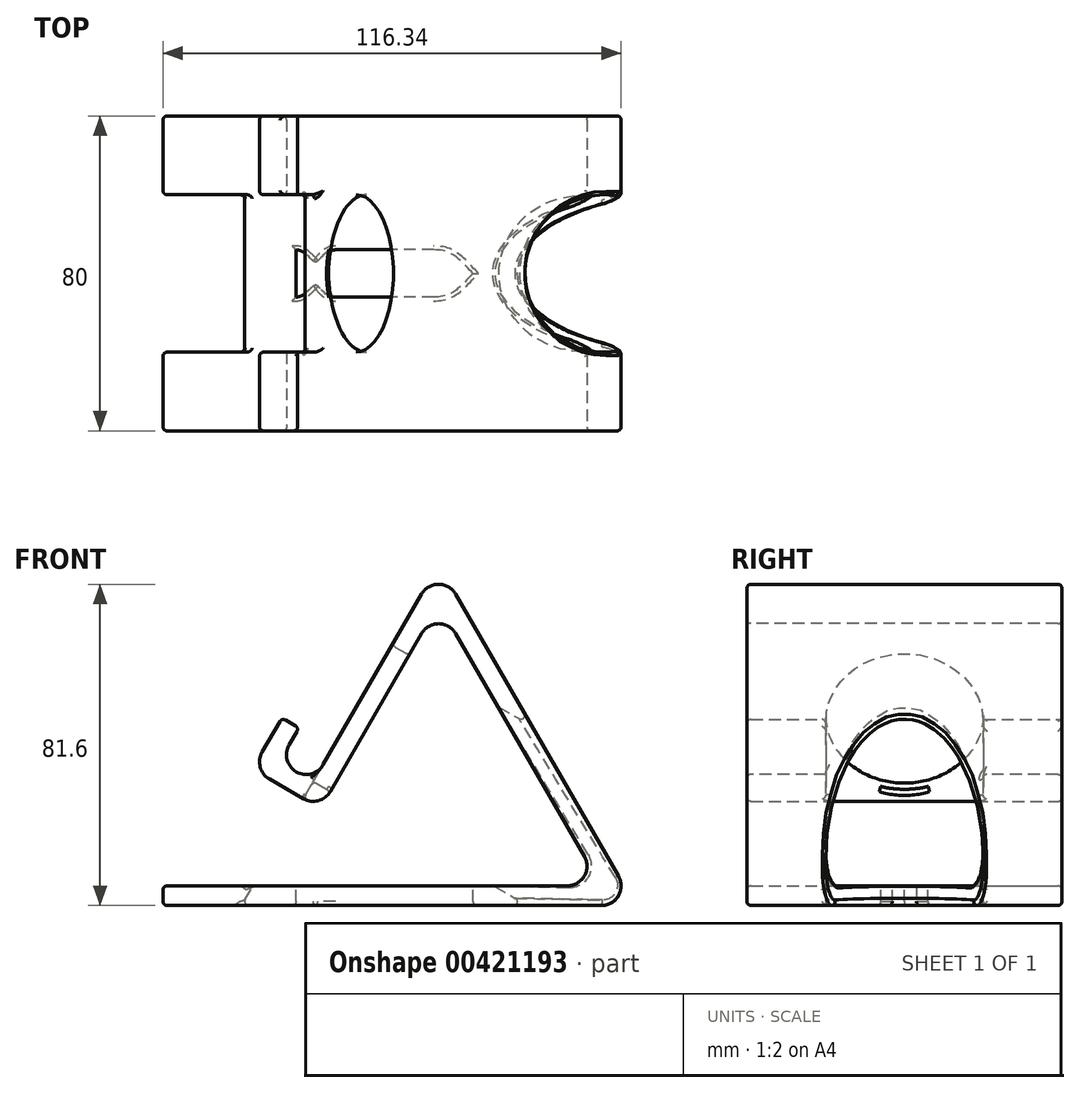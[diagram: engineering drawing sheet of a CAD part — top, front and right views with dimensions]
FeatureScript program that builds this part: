
annotation { "Feature Type Name" : "Feature", "Feature Type Description" : "" }
export const myFeature = defineFeature(function(context is Context, id is Id, definition is map)
    precondition{}
    {
        {
            var Q0;
            Q0=qCreatedBy(makeId("Front.planeOp"),FACE);
            var sketch = newSketch(context, id + "F0", { "sketchPlane" : qUnion([Q0])});
            skLineSegment(sketch, "E0", {"start": v(-70, -45.78) * mm, "end": v(50, -45.78) * mm});
            skLineSegment(sketch, "E1", {"start": v(50, -45.78) * mm, "end": v(0, 40.82) * mm});
            skLineSegment(sketch, "E2", {"start": v(0, 40.82) * mm, "end": v(-31.83, -14.3) * mm});
            skLineSegment(sketch, "E3", {"start": v(-31.83, -14.3) * mm, "end": v(-40.5, -9.3) * mm});
            skLineSegment(sketch, "E4", {"start": v(-40.5, -9.3) * mm, "end": v(-35.5, -0.65) * mm});
            skLineSegment(sketch, "E5", {"start": v(-35.5, -0.65) * mm, "end": v(-39.82, 1.85) * mm});
            skLineSegment(sketch, "E6", {"start": v(-39.82, 1.85) * mm, "end": v(-47.32, -11.14) * mm});
            skLineSegment(sketch, "E7", {"start": v(-47.32, -11.14) * mm, "end": v(-30, -21.14) * mm});
            skLineSegment(sketch, "E8", {"start": v(-30, -21.14) * mm, "end": v(0, 30.82) * mm});
            skLineSegment(sketch, "E9", {"start": v(0, 30.82) * mm, "end": v(41.34, -40.78) * mm});
            skLineSegment(sketch, "E10", {"start": v(41.34, -40.78) * mm, "end": v(-70, -40.78) * mm});
            skLineSegment(sketch, "E11", {"start": v(-70, -40.78) * mm, "end": v(-70, -45.78) * mm});
            skSolve(sketch);
        }
        {
            var Q0;
            Q0=makeQuery(id+"F0.imprint","IMPRINT",FACE,{"disambiguationData":[TD([[makeQuery(id+"F0.imprint","IMPRINT",EDGE,{"derivedFrom":sQuery(id+"F0.wireOp",EDGE,"E0")}),1.0]])]});
            extrude(context, id + "F1", {"entities" : qUnion([Q0]), "depth" : 80 * mm, "offsetDistance" : 25 * mm});
        }
        {
            var Q0;
            Q0=makeQuery(id+"F1.opExtrude","SWEPT_FACE",FACE,{"disambiguationData":[OSD([sQuery(id+"F0.wireOp",EDGE,"E3")])]});
            var sketch = newSketch(context, id + "F2", { "sketchPlane" : qUnion([Q0])});
            skLineSegment(sketch, "E12", {"start": v(-30.41, -40) * mm, "end": v(-20.41, -40) * mm});
            skLineSegment(sketch, "E13", {"start": v(-30.41, -40) * mm, "end": v(-30.41, -20) * mm});
            skLineSegment(sketch, "E14", {"start": v(-30.41, -20) * mm, "end": v(-20.41, -20) * mm});
            skLineSegment(sketch, "E15", {"start": v(-20.41, -20) * mm, "end": v(-20.41, -40) * mm});
            skLineSegment(sketch, "E16.MirrorCS", {"start": v(-20.41, -60) * mm, "end": v(-20.41, -40) * mm});
            skLineSegment(sketch, "E17.MirrorCS", {"start": v(-30.41, -40) * mm, "end": v(-30.41, -60) * mm});
            skLineSegment(sketch, "E18.MirrorCS", {"start": v(-30.41, -60) * mm, "end": v(-20.41, -60) * mm});
            skLineSegment(sketch, "E19", {"start": v(-30.41, -60) * mm, "end": v(-57.62, -60) * mm});
            skLineSegment(sketch, "E20", {"start": v(-57.62, -60) * mm, "end": v(-57.62, -20) * mm});
            skLineSegment(sketch, "E21", {"start": v(-57.62, -20) * mm, "end": v(-30.41, -20) * mm});
            skSolve(sketch);
        }
        {
            var Q0;
            Q0=makeQuery(id+"F2.imprint","IMPRINT",FACE,{"disambiguationData":[TD([[makeQuery(id+"F2.imprint","IMPRINT",EDGE,{"derivedFrom":sQuery(id+"F2.wireOp",EDGE,"E12")}),1.0]])]});
            var Q1;
            Q1=makeQuery(id+"F2.imprint","IMPRINT",FACE,{"disambiguationData":[TD([[makeQuery(id+"F2.imprint","IMPRINT",EDGE,{"derivedFrom":sQuery(id+"F2.wireOp",EDGE,"E12")}),-1.0]])]});
            var Q2;
            Q2=makeQuery(id+"F2.imprint","IMPRINT",FACE,{"disambiguationData":[TD([[makeQuery(id+"F2.imprint","IMPRINT",EDGE,{"derivedFrom":sQuery(id+"F2.wireOp",EDGE,"E13")}),1.0]])]});
            extrude(context, id + "F3", {"entities" : qUnion([Q0, Q1, Q2]), "operationType" : NewBodyOperationType.REMOVE, "oppositeDirection" : true, "depth" : 67.1 * mm, "offsetDistance" : 25 * mm, "hasSecondDirection" : true, "secondDirectionOppositeDirection" : false, "secondDirectionDepth" : 25 * mm});
        }
        {
            var Q0;
            Q0=makeQuery(id+"F1.opExtrude","SWEPT_FACE",FACE,{"disambiguationData":[OSD([sQuery(id+"F0.wireOp",EDGE,"E8")])]});
            var sketch = newSketch(context, id + "F4", { "sketchPlane" : qUnion([Q0])});
            skCircle(sketch, "E22", {"center": v(-40, -8.3) * mm, "radius": 20 * mm});
            skPoint(sketch, "E22.centerSnap0", {"position": v(-40, 26.7) * mm});
            skSolve(sketch);
        }
        {
            var Q0;
            Q0=makeQuery(id+"F4.imprint","IMPRINT",FACE,{"disambiguationData":[TD([[makeQuery(id+"F4.imprint","IMPRINT",EDGE,{"derivedFrom":sQuery(id+"F4.wireOp",EDGE,"E22")}),1.0]])]});
            extrude(context, id + "F5", {"entities" : qUnion([Q0]), "operationType" : NewBodyOperationType.REMOVE, "oppositeDirection" : true, "depth" : 25 * mm, "offsetDistance" : 25 * mm, "hasSecondDirection" : true, "secondDirectionOppositeDirection" : false, "secondDirectionDepth" : 129.4 * mm});
        }
        {
            var Q0;
            Q0=makeQuery(id+"F1.opExtrude","SWEPT_FACE",FACE,{"disambiguationData":[OSD([sQuery(id+"F0.wireOp",EDGE,"E10")])]});
            var sketch = newSketch(context, id + "F6", { "sketchPlane" : qUnion([Q0])});
            skPoint(sketch, "E23.0.internal.snap0", {"position": v(13.75, -40) * mm});
            skFitSpline(sketch, "E23", {"points": [v(8.75, -40) * mm, v(-1.25, -46) * mm], "startDerivative": vector(-10.6, -10.6) * mm, "endDerivative": vector(-15, 0) * mm});
            skLineSegment(sketch, "E24", {"start": v(8.75, -40) * mm, "end": v(-36.25, -40) * mm});
            skLineSegment(sketch, "E25", {"start": v(-1.25, -46) * mm, "end": v(-26.25, -46) * mm});
            skFitSpline(sketch, "E26", {"points": [v(-26.25, -46) * mm, v(-31.25, -43) * mm, v(-36.25, -46) * mm], "startDerivative": vector(-18, 0) * mm, "endDerivative": vector(-15, 0) * mm});
            skLineSegment(sketch, "E27", {"start": v(-36.25, -46) * mm, "end": v(-36.25, -40) * mm});
            skLineSegment(sketch, "E28", {"start": v(5.22, -43.54) * mm, "end": v(8.75, -40) * mm});
            skLineSegment(sketch, "E29.MirrorCS", {"start": v(5.22, -36.46) * mm, "end": v(8.75, -40) * mm});
            skFitSpline(sketch, "E30.MirrorCS", {"points": [v(-26.25, -34) * mm, v(-31.25, -37) * mm, v(-36.25, -34) * mm], "startDerivative": vector(-18, 0) * mm, "endDerivative": vector(-15, 0) * mm});
            skLineSegment(sketch, "E31.MirrorCS", {"start": v(-1.25, -34) * mm, "end": v(-26.25, -34) * mm});
            skLineSegment(sketch, "E32.MirrorCS", {"start": v(-36.25, -34) * mm, "end": v(-36.25, -40) * mm});
            skFitSpline(sketch, "E33.MirrorCS", {"points": [v(8.75, -40) * mm, v(-1.25, -34) * mm], "startDerivative": vector(-10.6, 10.6) * mm, "endDerivative": vector(-15, 0) * mm});
            skSolve(sketch);
        }
        {
            var Q0;
            Q0=makeQuery(id+"F6.imprint","IMPRINT",FACE,{"disambiguationData":[TD([[makeQuery(id+"F6.imprint","IMPRINT",EDGE,{"derivedFrom":sQuery(id+"F6.wireOp",EDGE,"E24")}),-1.0]])]});
            var Q1;
            Q1=makeQuery(id+"F6.imprint","IMPRINT",FACE,{"disambiguationData":[TD([[makeQuery(id+"F6.imprint","IMPRINT",EDGE,{"derivedFrom":sQuery(id+"F6.wireOp",EDGE,"E23")}),-1.0]])]});
            extrude(context, id + "F7", {"entities" : qUnion([Q0, Q1]), "operationType" : NewBodyOperationType.REMOVE, "oppositeDirection" : true, "depth" : 25 * mm, "offsetDistance" : 25 * mm});
        }
        {
            var Q0;
            Q0=makeQuery(id+"F1.opExtrude","SWEPT_EDGE",EDGE,{"disambiguationData":[OSD([sQuery(id+"F0.wireOp",EDGE,"E1"),sQuery(id+"F0.wireOp",EDGE,"E2")])]});
            var Q1;
            Q1=makeQuery(id+"F1.opExtrude","SWEPT_EDGE",EDGE,{"disambiguationData":[OSD([sQuery(id+"F0.wireOp",EDGE,"E8"),sQuery(id+"F0.wireOp",EDGE,"E9")])]});
            var Q2;
            {var subQ0=sQuery(id+"F0.wireOp",EDGE,"E0");var subQ1=sQuery(id+"F0.wireOp",EDGE,"E1");Q2=makeQuery(id+"F5.boolean.opBoolean","SPLIT",EDGE,{"disambiguationData":[TD([makeQuery(id+"F1.opExtrude","CAP_FACE",FACE,{"disambiguationData":[OSD([subQ0,subQ1,sQuery(id+"F0.wireOp",EDGE,"E2"),sQuery(id+"F0.wireOp",EDGE,"E3"),sQuery(id+"F0.wireOp",EDGE,"E4"),sQuery(id+"F0.wireOp",EDGE,"E5"),sQuery(id+"F0.wireOp",EDGE,"E6"),sQuery(id+"F0.wireOp",EDGE,"E7"),sQuery(id+"F0.wireOp",EDGE,"E8"),sQuery(id+"F0.wireOp",EDGE,"E9"),sQuery(id+"F0.wireOp",EDGE,"E10"),sQuery(id+"F0.wireOp",EDGE,"E11")])],"isStart":false})])],"derivedFrom":makeQuery(id+"F1.opExtrude","SWEPT_EDGE",EDGE,{"disambiguationData":[OSD([subQ0,subQ1])]})});}
            var Q3;
            {var subQ0=sQuery(id+"F0.wireOp",EDGE,"E0");var subQ1=sQuery(id+"F0.wireOp",EDGE,"E1");Q3=makeQuery(id+"F5.boolean.opBoolean","SPLIT",EDGE,{"disambiguationData":[TD([makeQuery(id+"F1.opExtrude","CAP_FACE",FACE,{"disambiguationData":[OSD([subQ0,subQ1,sQuery(id+"F0.wireOp",EDGE,"E2"),sQuery(id+"F0.wireOp",EDGE,"E3"),sQuery(id+"F0.wireOp",EDGE,"E4"),sQuery(id+"F0.wireOp",EDGE,"E5"),sQuery(id+"F0.wireOp",EDGE,"E6"),sQuery(id+"F0.wireOp",EDGE,"E7"),sQuery(id+"F0.wireOp",EDGE,"E8"),sQuery(id+"F0.wireOp",EDGE,"E9"),sQuery(id+"F0.wireOp",EDGE,"E10"),sQuery(id+"F0.wireOp",EDGE,"E11")])],"isStart":true})])],"derivedFrom":makeQuery(id+"F1.opExtrude","SWEPT_EDGE",EDGE,{"disambiguationData":[OSD([subQ0,subQ1])]})});}
            var Q4;
            {var subQ0=sQuery(id+"F0.wireOp",EDGE,"E10");var subQ1=sQuery(id+"F0.wireOp",EDGE,"E9");Q4=makeQuery(id+"F5.boolean.opBoolean","SPLIT",EDGE,{"disambiguationData":[TD([makeQuery(id+"F1.opExtrude","CAP_FACE",FACE,{"disambiguationData":[OSD([sQuery(id+"F0.wireOp",EDGE,"E0"),sQuery(id+"F0.wireOp",EDGE,"E1"),sQuery(id+"F0.wireOp",EDGE,"E2"),sQuery(id+"F0.wireOp",EDGE,"E3"),sQuery(id+"F0.wireOp",EDGE,"E4"),sQuery(id+"F0.wireOp",EDGE,"E5"),sQuery(id+"F0.wireOp",EDGE,"E6"),sQuery(id+"F0.wireOp",EDGE,"E7"),sQuery(id+"F0.wireOp",EDGE,"E8"),subQ1,subQ0,sQuery(id+"F0.wireOp",EDGE,"E11")])],"isStart":false})])],"derivedFrom":makeQuery(id+"F1.opExtrude","SWEPT_EDGE",EDGE,{"disambiguationData":[OSD([subQ1,subQ0])]})});}
            var Q5;
            {var subQ0=sQuery(id+"F0.wireOp",EDGE,"E10");var subQ1=sQuery(id+"F0.wireOp",EDGE,"E9");Q5=makeQuery(id+"F5.boolean.opBoolean","SPLIT",EDGE,{"disambiguationData":[TD([makeQuery(id+"F1.opExtrude","CAP_FACE",FACE,{"disambiguationData":[OSD([sQuery(id+"F0.wireOp",EDGE,"E0"),sQuery(id+"F0.wireOp",EDGE,"E1"),sQuery(id+"F0.wireOp",EDGE,"E2"),sQuery(id+"F0.wireOp",EDGE,"E3"),sQuery(id+"F0.wireOp",EDGE,"E4"),sQuery(id+"F0.wireOp",EDGE,"E5"),sQuery(id+"F0.wireOp",EDGE,"E6"),sQuery(id+"F0.wireOp",EDGE,"E7"),sQuery(id+"F0.wireOp",EDGE,"E8"),subQ1,subQ0,sQuery(id+"F0.wireOp",EDGE,"E11")])],"isStart":true})])],"derivedFrom":makeQuery(id+"F1.opExtrude","SWEPT_EDGE",EDGE,{"disambiguationData":[OSD([subQ1,subQ0])]})});}
            var Q6;
            Q6=makeQuery(id+"F1.opExtrude","SWEPT_EDGE",EDGE,{"disambiguationData":[OSD([sQuery(id+"F0.wireOp",EDGE,"E7"),sQuery(id+"F0.wireOp",EDGE,"E8")])]});
            var Q7;
            {var subQ0=sQuery(id+"F0.wireOp",EDGE,"E2");var subQ1=sQuery(id+"F0.wireOp",EDGE,"E3");Q7=makeQuery(id+"F3.boolean.opBoolean","SPLIT",EDGE,{"disambiguationData":[TD([makeQuery(id+"F3.opExtrude","SWEPT_FACE",FACE,{"disambiguationData":[OSD([sQuery(id+"F2.wireOp",EDGE,"E18.MirrorCS"),sQuery(id+"F2.wireOp",EDGE,"E19")])]})])],"derivedFrom":makeQuery(id+"F1.opExtrude","SWEPT_EDGE",EDGE,{"disambiguationData":[OSD([subQ0,subQ1])]})});}
            var Q8;
            {var subQ0=sQuery(id+"F0.wireOp",EDGE,"E3");var subQ1=sQuery(id+"F0.wireOp",EDGE,"E2");Q8=makeQuery(id+"F3.boolean.opBoolean","SPLIT",EDGE,{"disambiguationData":[TD([makeQuery(id+"F3.opExtrude","SWEPT_FACE",FACE,{"disambiguationData":[OSD([sQuery(id+"F2.wireOp",EDGE,"E14"),sQuery(id+"F2.wireOp",EDGE,"E21")])]})])],"derivedFrom":makeQuery(id+"F1.opExtrude","SWEPT_EDGE",EDGE,{"disambiguationData":[OSD([subQ1,subQ0])]})});}
            var Q9;
            {var subQ0=sQuery(id+"F0.wireOp",EDGE,"E4");var subQ1=sQuery(id+"F0.wireOp",EDGE,"E3");Q9=makeQuery(id+"F3.boolean.opBoolean","SPLIT",EDGE,{"disambiguationData":[TD([makeQuery(id+"F3.opExtrude","SWEPT_FACE",FACE,{"disambiguationData":[OSD([sQuery(id+"F2.wireOp",EDGE,"E18.MirrorCS"),sQuery(id+"F2.wireOp",EDGE,"E19")])]})])],"derivedFrom":makeQuery(id+"F1.opExtrude","SWEPT_EDGE",EDGE,{"disambiguationData":[OSD([subQ1,subQ0])]})});}
            var Q10;
            {var subQ0=sQuery(id+"F0.wireOp",EDGE,"E4");var subQ1=sQuery(id+"F0.wireOp",EDGE,"E3");Q10=makeQuery(id+"F3.boolean.opBoolean","SPLIT",EDGE,{"disambiguationData":[TD([makeQuery(id+"F3.opExtrude","SWEPT_FACE",FACE,{"disambiguationData":[OSD([sQuery(id+"F2.wireOp",EDGE,"E14"),sQuery(id+"F2.wireOp",EDGE,"E21")])]})])],"derivedFrom":makeQuery(id+"F1.opExtrude","SWEPT_EDGE",EDGE,{"disambiguationData":[OSD([subQ1,subQ0])]})});}
            var Q11;
            {var subQ0=sQuery(id+"F0.wireOp",EDGE,"E7");var subQ1=sQuery(id+"F0.wireOp",EDGE,"E6");Q11=makeQuery(id+"F3.boolean.opBoolean","SPLIT",EDGE,{"disambiguationData":[TD([makeQuery(id+"F3.opExtrude","SWEPT_FACE",FACE,{"disambiguationData":[OSD([sQuery(id+"F2.wireOp",EDGE,"E14"),sQuery(id+"F2.wireOp",EDGE,"E21")])]})])],"derivedFrom":makeQuery(id+"F1.opExtrude","SWEPT_EDGE",EDGE,{"disambiguationData":[OSD([subQ1,subQ0])]})});}
            var Q12;
            {var subQ0=sQuery(id+"F0.wireOp",EDGE,"E7");var subQ1=sQuery(id+"F0.wireOp",EDGE,"E6");Q12=makeQuery(id+"F3.boolean.opBoolean","SPLIT",EDGE,{"disambiguationData":[TD([makeQuery(id+"F3.opExtrude","SWEPT_FACE",FACE,{"disambiguationData":[OSD([sQuery(id+"F2.wireOp",EDGE,"E18.MirrorCS"),sQuery(id+"F2.wireOp",EDGE,"E19")])]})])],"derivedFrom":makeQuery(id+"F1.opExtrude","SWEPT_EDGE",EDGE,{"disambiguationData":[OSD([subQ1,subQ0])]})});}
            fillet(context, id + "F8", {"entities" : qUnion([Q0, Q1, Q2, Q3, Q4, Q5, Q6, Q7, Q8, Q9, Q10, Q11, Q12]), "radius" : 5 * mm, "tangentPropagation" : true, "allowEdgeOverflow" : false});
        }
        {
            var Q0;
            Q0=makeQuery(id+"F1.opExtrude","CAP_EDGE",EDGE,{"disambiguationData":[OSD([sQuery(id+"F0.wireOp",EDGE,"E2")])],"isStart":false});
            var Q1;
            {var subQ0=sQuery(id+"F0.wireOp",EDGE,"E9");var subQ1=sQuery(id+"F0.wireOp",EDGE,"E8");Q1=makeQuery(id+"F8.opFillet","BLEND_EDGE",EDGE,{"blendedFrom":[makeQuery(id+"F1.opExtrude","SWEPT_EDGE",EDGE,{"disambiguationData":[OSD([subQ1,subQ0])]}),makeQuery(id+"F1.opExtrude","CAP_FACE",FACE,{"disambiguationData":[OSD([sQuery(id+"F0.wireOp",EDGE,"E0"),sQuery(id+"F0.wireOp",EDGE,"E1"),sQuery(id+"F0.wireOp",EDGE,"E2"),sQuery(id+"F0.wireOp",EDGE,"E3"),sQuery(id+"F0.wireOp",EDGE,"E4"),sQuery(id+"F0.wireOp",EDGE,"E5"),sQuery(id+"F0.wireOp",EDGE,"E6"),sQuery(id+"F0.wireOp",EDGE,"E7"),subQ1,subQ0,sQuery(id+"F0.wireOp",EDGE,"E10"),sQuery(id+"F0.wireOp",EDGE,"E11")])],"isStart":false})],"blendedInto":[makeQuery(id+"F1.opExtrude","CAP_FACE",FACE,{"disambiguationData":[OSD([sQuery(id+"F0.wireOp",EDGE,"E0"),sQuery(id+"F0.wireOp",EDGE,"E1"),sQuery(id+"F0.wireOp",EDGE,"E2"),sQuery(id+"F0.wireOp",EDGE,"E3"),sQuery(id+"F0.wireOp",EDGE,"E4"),sQuery(id+"F0.wireOp",EDGE,"E5"),sQuery(id+"F0.wireOp",EDGE,"E6"),sQuery(id+"F0.wireOp",EDGE,"E7"),subQ1,subQ0,sQuery(id+"F0.wireOp",EDGE,"E10"),sQuery(id+"F0.wireOp",EDGE,"E11")])],"isStart":false})]});}
            var Q2;
            Q2=makeQuery(id+"F1.opExtrude","CAP_EDGE",EDGE,{"disambiguationData":[OSD([sQuery(id+"F0.wireOp",EDGE,"E6")])],"isStart":false});
            var Q3;
            Q3=makeQuery(id+"F1.opExtrude","CAP_EDGE",EDGE,{"disambiguationData":[OSD([sQuery(id+"F0.wireOp",EDGE,"E9")])],"isStart":true});
            var Q4;
            Q4=makeQuery(id+"F1.opExtrude","CAP_EDGE",EDGE,{"disambiguationData":[OSD([sQuery(id+"F0.wireOp",EDGE,"E1")])],"isStart":true});
            var Q5;
            {var subQ0=sQuery(id+"F0.wireOp",EDGE,"E5");var subQ1=sQuery(id+"F0.wireOp",EDGE,"E4");Q5=makeQuery(id+"F3.boolean.opBoolean","SPLIT",EDGE,{"disambiguationData":[TD([makeQuery(id+"F3.opExtrude","SWEPT_FACE",FACE,{"disambiguationData":[OSD([sQuery(id+"F2.wireOp",EDGE,"E14"),sQuery(id+"F2.wireOp",EDGE,"E21")])]})])],"derivedFrom":makeQuery(id+"F1.opExtrude","SWEPT_EDGE",EDGE,{"disambiguationData":[OSD([subQ1,subQ0])]})});}
            var Q6;
            Q6=makeQuery(id+"F3.boolean.opBoolean","INTERSECT",EDGE,{"derivedFrom":[makeQuery(id+"F1.opExtrude","SWEPT_FACE",FACE,{"disambiguationData":[OSD([sQuery(id+"F0.wireOp",EDGE,"E4")])]}),makeQuery(id+"F3.opExtrude","SWEPT_FACE",FACE,{"disambiguationData":[OSD([sQuery(id+"F2.wireOp",EDGE,"E14"),sQuery(id+"F2.wireOp",EDGE,"E21")])]})]});
            var Q7;
            Q7=makeQuery(id+"F3.boolean.opBoolean","INTERSECT",EDGE,{"derivedFrom":[makeQuery(id+"F1.opExtrude","SWEPT_FACE",FACE,{"disambiguationData":[OSD([sQuery(id+"F0.wireOp",EDGE,"E6")])]}),makeQuery(id+"F3.opExtrude","SWEPT_FACE",FACE,{"disambiguationData":[OSD([sQuery(id+"F2.wireOp",EDGE,"E14"),sQuery(id+"F2.wireOp",EDGE,"E21")])]})]});
            var Q8;
            {var subQ0=sQuery(id+"F0.wireOp",EDGE,"E6");var subQ1=sQuery(id+"F0.wireOp",EDGE,"E5");Q8=makeQuery(id+"F3.boolean.opBoolean","SPLIT",EDGE,{"disambiguationData":[TD([makeQuery(id+"F3.opExtrude","SWEPT_FACE",FACE,{"disambiguationData":[OSD([sQuery(id+"F2.wireOp",EDGE,"E14"),sQuery(id+"F2.wireOp",EDGE,"E21")])]})])],"derivedFrom":makeQuery(id+"F1.opExtrude","SWEPT_EDGE",EDGE,{"disambiguationData":[OSD([subQ1,subQ0])]})});}
            var Q9;
            Q9=makeQuery(id+"F1.opExtrude","CAP_EDGE",EDGE,{"disambiguationData":[OSD([sQuery(id+"F0.wireOp",EDGE,"E6")])],"isStart":true});
            var Q10;
            Q10=makeQuery(id+"F3.boolean.opBoolean","INTERSECT",EDGE,{"derivedFrom":[makeQuery(id+"F1.opExtrude","SWEPT_FACE",FACE,{"disambiguationData":[OSD([sQuery(id+"F0.wireOp",EDGE,"E7")])]}),makeQuery(id+"F3.opExtrude","SWEPT_FACE",FACE,{"disambiguationData":[OSD([sQuery(id+"F2.wireOp",EDGE,"E14"),sQuery(id+"F2.wireOp",EDGE,"E21")])]})]});
            var Q11;
            Q11=makeQuery(id+"F8.opFillet","BLEND_EDGE",EDGE,{"blendedFrom":[makeQuery(id+"F1.opExtrude","SWEPT_EDGE",EDGE,{"disambiguationData":[OSD([sQuery(id+"F0.wireOp",EDGE,"E7"),sQuery(id+"F0.wireOp",EDGE,"E8")])]}),makeQuery(id+"F3.boolean.opBoolean","MERGE",FACE,{"derivedFrom":[makeQuery(id+"F1.opExtrude","SWEPT_FACE",FACE,{"disambiguationData":[OSD([sQuery(id+"F0.wireOp",EDGE,"E2")])]}),makeQuery(id+"F3.opExtrude","SWEPT_FACE",FACE,{"disambiguationData":[OSD([sQuery(id+"F2.wireOp",EDGE,"E15"),sQuery(id+"F2.wireOp",EDGE,"E16.MirrorCS")])]})]})],"blendedInto":[makeQuery(id+"F3.boolean.opBoolean","MERGE",FACE,{"derivedFrom":[makeQuery(id+"F1.opExtrude","SWEPT_FACE",FACE,{"disambiguationData":[OSD([sQuery(id+"F0.wireOp",EDGE,"E2")])]}),makeQuery(id+"F3.opExtrude","SWEPT_FACE",FACE,{"disambiguationData":[OSD([sQuery(id+"F2.wireOp",EDGE,"E15"),sQuery(id+"F2.wireOp",EDGE,"E16.MirrorCS")])]})]})]});
            var Q12;
            Q12=makeQuery(id+"F3.boolean.opBoolean","INTERSECT",EDGE,{"derivedFrom":[makeQuery(id+"F1.opExtrude","SWEPT_FACE",FACE,{"disambiguationData":[OSD([sQuery(id+"F0.wireOp",EDGE,"E7")])]}),makeQuery(id+"F3.opExtrude","SWEPT_FACE",FACE,{"disambiguationData":[OSD([sQuery(id+"F2.wireOp",EDGE,"E18.MirrorCS"),sQuery(id+"F2.wireOp",EDGE,"E19")])]})]});
            var Q13;
            Q13=makeQuery(id+"F3.boolean.opBoolean","INTERSECT",EDGE,{"derivedFrom":[makeQuery(id+"F1.opExtrude","SWEPT_FACE",FACE,{"disambiguationData":[OSD([sQuery(id+"F0.wireOp",EDGE,"E6")])]}),makeQuery(id+"F3.opExtrude","SWEPT_FACE",FACE,{"disambiguationData":[OSD([sQuery(id+"F2.wireOp",EDGE,"E18.MirrorCS"),sQuery(id+"F2.wireOp",EDGE,"E19")])]})]});
            var Q14;
            {var subQ0=sQuery(id+"F0.wireOp",EDGE,"E6");var subQ1=sQuery(id+"F0.wireOp",EDGE,"E5");Q14=makeQuery(id+"F3.boolean.opBoolean","SPLIT",EDGE,{"disambiguationData":[TD([makeQuery(id+"F3.opExtrude","SWEPT_FACE",FACE,{"disambiguationData":[OSD([sQuery(id+"F2.wireOp",EDGE,"E18.MirrorCS"),sQuery(id+"F2.wireOp",EDGE,"E19")])]})])],"derivedFrom":makeQuery(id+"F1.opExtrude","SWEPT_EDGE",EDGE,{"disambiguationData":[OSD([subQ1,subQ0])]})});}
            var Q15;
            Q15=makeQuery(id+"F3.boolean.opBoolean","INTERSECT",EDGE,{"derivedFrom":[makeQuery(id+"F1.opExtrude","SWEPT_FACE",FACE,{"disambiguationData":[OSD([sQuery(id+"F0.wireOp",EDGE,"E5")])]}),makeQuery(id+"F3.opExtrude","SWEPT_FACE",FACE,{"disambiguationData":[OSD([sQuery(id+"F2.wireOp",EDGE,"E18.MirrorCS"),sQuery(id+"F2.wireOp",EDGE,"E19")])]})]});
            var Q16;
            {var subQ0=sQuery(id+"F0.wireOp",EDGE,"E5");var subQ1=sQuery(id+"F0.wireOp",EDGE,"E4");Q16=makeQuery(id+"F3.boolean.opBoolean","SPLIT",EDGE,{"disambiguationData":[TD([makeQuery(id+"F3.opExtrude","SWEPT_FACE",FACE,{"disambiguationData":[OSD([sQuery(id+"F2.wireOp",EDGE,"E18.MirrorCS"),sQuery(id+"F2.wireOp",EDGE,"E19")])]})])],"derivedFrom":makeQuery(id+"F1.opExtrude","SWEPT_EDGE",EDGE,{"disambiguationData":[OSD([subQ1,subQ0])]})});}
            var Q17;
            Q17=makeQuery(id+"F1.opExtrude","CAP_EDGE",EDGE,{"disambiguationData":[OSD([sQuery(id+"F0.wireOp",EDGE,"E5")])],"isStart":false});
            var Q18;
            Q18=makeQuery(id+"F5.boolean.opBoolean","INTERSECT",EDGE,{"derivedFrom":[makeQuery(id+"F3.boolean.opBoolean","MERGE",FACE,{"derivedFrom":[makeQuery(id+"F1.opExtrude","SWEPT_FACE",FACE,{"disambiguationData":[OSD([sQuery(id+"F0.wireOp",EDGE,"E2")])]}),makeQuery(id+"F3.opExtrude","SWEPT_FACE",FACE,{"disambiguationData":[OSD([sQuery(id+"F2.wireOp",EDGE,"E15"),sQuery(id+"F2.wireOp",EDGE,"E16.MirrorCS")])]})]}),makeQuery(id+"F5.opExtrude","SWEPT_FACE",FACE,{"disambiguationData":[OSD([sQuery(id+"F4.wireOp",EDGE,"E22")])]})]});
            var Q19;
            Q19=makeQuery(id+"F5.boolean.opBoolean","COPY",FACE,{"disambiguationData":[TD([makeQuery(id+"F1.opExtrude","SWEPT_FACE",FACE,{"disambiguationData":[OSD([sQuery(id+"F0.wireOp",EDGE,"E2")])]})])],"derivedFrom":makeQuery(id+"F5.opExtrude","SWEPT_FACE",FACE,{"disambiguationData":[OSD([sQuery(id+"F4.wireOp",EDGE,"E22")])]})});
            var Q20;
            Q20=makeQuery(id+"F5.boolean.opBoolean","COPY",FACE,{"disambiguationData":[TD([makeQuery(id+"F1.opExtrude","SWEPT_FACE",FACE,{"disambiguationData":[OSD([sQuery(id+"F0.wireOp",EDGE,"E0")])]})])],"derivedFrom":makeQuery(id+"F5.opExtrude","SWEPT_FACE",FACE,{"disambiguationData":[OSD([sQuery(id+"F4.wireOp",EDGE,"E22")])]})});
            var Q21;
            Q21=makeQuery(id+"F3.boolean.opBoolean","COPY",FACE,{"derivedFrom":makeQuery(id+"F3.opExtrude","SWEPT_FACE",FACE,{"disambiguationData":[OSD([sQuery(id+"F2.wireOp",EDGE,"E15"),sQuery(id+"F2.wireOp",EDGE,"E16.MirrorCS")])]})});
            var Q22;
            {var subQ1=sQuery(id+"F0.wireOp",EDGE,"E11");Q22=makeQuery(id+"F3.boolean.opBoolean","SPLIT",FACE,{"disambiguationData":[TD([makeQuery(id+"F3.opExtrude","SWEPT_FACE",FACE,{"disambiguationData":[OSD([sQuery(id+"F2.wireOp",EDGE,"E18.MirrorCS"),sQuery(id+"F2.wireOp",EDGE,"E19")])]})])],"derivedFrom":makeQuery(id+"F1.opExtrude","SWEPT_FACE",FACE,{"disambiguationData":[OSD([subQ1])]})});}
            var Q23;
            {var subQ1=sQuery(id+"F0.wireOp",EDGE,"E11");Q23=makeQuery(id+"F3.boolean.opBoolean","SPLIT",FACE,{"disambiguationData":[TD([makeQuery(id+"F3.opExtrude","SWEPT_FACE",FACE,{"disambiguationData":[OSD([sQuery(id+"F2.wireOp",EDGE,"E14"),sQuery(id+"F2.wireOp",EDGE,"E21")])]})])],"derivedFrom":makeQuery(id+"F1.opExtrude","SWEPT_FACE",FACE,{"disambiguationData":[OSD([subQ1])]})});}
            var Q24;
            {var subQ0=sQuery(id+"F0.wireOp",EDGE,"E2");var subQ1=sQuery(id+"F2.wireOp",EDGE,"E14");var subQ2=sQuery(id+"F2.wireOp",EDGE,"E15");Q24=makeQuery(id+"F3.boolean.opBoolean","COPY",EDGE,{"disambiguationData":[topologyDisambiguationEdgeConnected([makeQuery(id+"F1.opExtrude","SWEPT_FACE",FACE,{"disambiguationData":[OSD([subQ0])]}),makeQuery(id+"F3.opExtrude","SWEPT_FACE",FACE,{"disambiguationData":[OSD([subQ1,sQuery(id+"F2.wireOp",EDGE,"E21")])]}),makeQuery(id+"F3.opExtrude","SWEPT_FACE",FACE,{"disambiguationData":[OSD([subQ2,sQuery(id+"F2.wireOp",EDGE,"E16.MirrorCS")])]})])],"derivedFrom":makeQuery(id+"F3.opExtrude","SWEPT_EDGE",EDGE,{"disambiguationData":[OSD([subQ0,sQuery(id+"F0.wireOp",EDGE,"E3"),subQ1,subQ2])]})});}
            var Q25;
            {var subQ0=sQuery(id+"F0.wireOp",EDGE,"E2");var subQ1=sQuery(id+"F2.wireOp",EDGE,"E16.MirrorCS");var subQ2=sQuery(id+"F2.wireOp",EDGE,"E18.MirrorCS");Q25=makeQuery(id+"F3.boolean.opBoolean","COPY",EDGE,{"disambiguationData":[topologyDisambiguationEdgeConnected([makeQuery(id+"F1.opExtrude","SWEPT_FACE",FACE,{"disambiguationData":[OSD([subQ0])]}),makeQuery(id+"F3.opExtrude","SWEPT_FACE",FACE,{"disambiguationData":[OSD([sQuery(id+"F2.wireOp",EDGE,"E15"),subQ1])]}),makeQuery(id+"F3.opExtrude","SWEPT_FACE",FACE,{"disambiguationData":[OSD([subQ2,sQuery(id+"F2.wireOp",EDGE,"E19")])]})])],"derivedFrom":makeQuery(id+"F3.opExtrude","SWEPT_EDGE",EDGE,{"disambiguationData":[OSD([subQ0,sQuery(id+"F0.wireOp",EDGE,"E3"),subQ1,subQ2])]})});}
            var Q26;
            Q26=makeQuery(id+"F3.boolean.opBoolean","INTERSECT",EDGE,{"derivedFrom":[makeQuery(id+"F1.opExtrude","SWEPT_FACE",FACE,{"disambiguationData":[OSD([sQuery(id+"F0.wireOp",EDGE,"E3")])]}),makeQuery(id+"F3.opExtrude","SWEPT_FACE",FACE,{"disambiguationData":[OSD([sQuery(id+"F2.wireOp",EDGE,"E18.MirrorCS"),sQuery(id+"F2.wireOp",EDGE,"E19")])]})]});
            var Q27;
            Q27=makeQuery(id+"F7.boolean.opBoolean","COPY",EDGE,{"derivedFrom":makeQuery(id+"F7.opExtrude","CAP_EDGE",EDGE,{"disambiguationData":[OSD([sQuery(id+"F6.wireOp",EDGE,"E31.MirrorCS")])],"isStart":true})});
            var Q28;
            Q28=makeQuery(id+"F7.boolean.opBoolean","COPY",EDGE,{"derivedFrom":makeQuery(id+"F7.opExtrude","CAP_EDGE",EDGE,{"disambiguationData":[OSD([sQuery(id+"F6.wireOp",EDGE,"E25")])],"isStart":true})});
            var Q29;
            Q29=makeQuery(id+"F7.boolean.opBoolean","INTERSECT",EDGE,{"derivedFrom":[makeQuery(id+"F1.opExtrude","SWEPT_FACE",FACE,{"disambiguationData":[OSD([sQuery(id+"F0.wireOp",EDGE,"E0")])]}),makeQuery(id+"F7.opExtrude","SWEPT_FACE",FACE,{"disambiguationData":[OSD([sQuery(id+"F6.wireOp",EDGE,"E31.MirrorCS")])]})]});
            var Q30;
            Q30=makeQuery(id+"F7.boolean.opBoolean","INTERSECT",EDGE,{"derivedFrom":[makeQuery(id+"F1.opExtrude","SWEPT_FACE",FACE,{"disambiguationData":[OSD([sQuery(id+"F0.wireOp",EDGE,"E0")])]}),makeQuery(id+"F7.opExtrude","SWEPT_FACE",FACE,{"disambiguationData":[OSD([sQuery(id+"F6.wireOp",EDGE,"E25")])]})]});
            var Q31;
            Q31=makeQuery(id+"F7.boolean.opBoolean","COPY",EDGE,{"derivedFrom":makeQuery(id+"F7.opExtrude","CAP_EDGE",EDGE,{"disambiguationData":[OSD([sQuery(id+"F6.wireOp",EDGE,"E27"),sQuery(id+"F6.wireOp",EDGE,"E32.MirrorCS")])],"isStart":true})});
            var Q32;
            Q32=makeQuery(id+"F7.boolean.opBoolean","INTERSECT",EDGE,{"derivedFrom":[makeQuery(id+"F1.opExtrude","SWEPT_FACE",FACE,{"disambiguationData":[OSD([sQuery(id+"F0.wireOp",EDGE,"E0")])]}),makeQuery(id+"F7.opExtrude","SWEPT_FACE",FACE,{"disambiguationData":[OSD([sQuery(id+"F6.wireOp",EDGE,"E27"),sQuery(id+"F6.wireOp",EDGE,"E32.MirrorCS")])]})]});
            fillet(context, id + "F9", {"entities" : qUnion([Q0, Q1, Q2, Q3, Q4, Q5, Q6, Q7, Q8, Q9, Q10, Q11, Q12, Q13, Q14, Q15, Q16, Q17, Q18, Q19, Q20, Q21, Q22, Q23, Q24, Q25, Q26, Q27, Q28, Q29, Q30, Q31, Q32]), "radius" : 1 * mm, "tangentPropagation" : true, "allowEdgeOverflow" : false});
        }
    });
